# Revit family: Sanitary_Accessories_hansgrohe_40512XXX-Logis-Towel-holder-twin-handle
name_source: partatom
category: Furniture
revit_build: Autodesk Revit 2018 (Build: 20190510_1515(x64)
units: mm (PartAtom-declared; Revit-internal decimal feet)

## family parameters
Always vertical = No
Cut with Voids When Loaded = No
OmniClass Number = 23.31.25.25
OmniClass Title = Towel Bars
Room Calculation Point = No
Shared = No
Work Plane-Based = Yes

## types (2) — shared parameters
Always visible = Yes
BIMobject category = Accessories
Default Elevation = 1219.2 mm  [stored 4 ft]
Description = Logis Towel holder twin-handle
Design country = Germany
EAN code = 4011097584584
Edition number = 1
GTIN code = https://4011097584584
IFC Classification = Furnishing Element
Manufacturer = Hansgrohe
Manufacturer country = Germany
Manufacturer name = hansgrohe
Material main = Brass
Material secondary = Chrome
Model = 40512XXX
OmniClass Code = 23-31 25 25
OmniClass Description = Towel Bars
Product Guid = 92c25a05-0cfa-424a-9f3e-d527f7d96907
Product SKU = 40512XXX
Product data url = https://bimobject.com
Product family = Logis
Product group = Towel holder
Product name = 40512XXX Logis Towel holder twin-handle
Product url = https://www.hansgrohe.com
QR code = https://bimobject.com
URL = https://www.hansgrohe.com
Weight Net (Kg) = 1.1

## per-type parameters (varying)
| type | Material |
| 000 Chrome | Hansgrohe - Metal - 000 Chrome |
| 820 Brushed Nickel | Hansgrohe - Metal - 820 Brushed Nickel |

note: [stored X ft] marks values corroborated as IEEE doubles in the binary element streams (Revit-internal decimal feet)

## geometry (parser evidence)
native form markers: Blend x2, Sweep x3
no freeform markers — native parametric forms only
